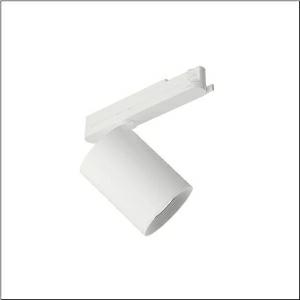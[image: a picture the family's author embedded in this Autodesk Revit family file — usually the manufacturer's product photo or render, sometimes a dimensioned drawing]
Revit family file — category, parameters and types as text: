
# Revit family: spot_21_51se12mba5b
name_source: partatom
category: Lighting Fixtures
units: mm (PartAtom-declared; Revit-internal decimal feet)

## family parameters
Cut with Voids When Loaded = No
Host = Face
Light Source = No
Part Type = Normal
Room Calculation Point = No
Round Connector Dimension = Use Diameter
Shared = No

## types (1)
- --- (1 x LED, 5240 lm, 41.7 W, 2700K)
    Apparent Load = 42 VA
    CIE Flux Codes = 95 98 99 100 100
    Color Rendering = 90
    Color Temperature = 2700K
    Default Elevation = 1800 mm
    Description = Spot 21, directional spotlight, light control with lens, of PMMA, LED rated luminous flux: 5.040lm, light colour: 927, control gear: ECG Multilumen, with 3-phase adapter, mains connection: 220..240V, AC, 50/60Hz, of aluminium, traffic white (RAL 9016), length: 213mm, diameter: 105mm, protection rating (complete): IP20, insulation class (complete): insulation class I (protective earthing), certification: CE, impact resistance: IK02, permissible ambient temperature for indoor applications: -20..+40°C, packaging unit: 1 piece
    Height = 175 mm
    Lamp = 1 x LED
    Lamp Light Flux = 5240 lm
    Lamp Power = 41.7 W
    Lamp count = 1
    Length = 105 mm
    Luminous efficacy = 126 lm/W
    Manufacturer = Siteco
    ModVariant = No
    Model = 51SE12MBA5B
    Mounting Place = Ceiling
    Mounting Type = Pendant
    Number of Poles = 1
    OnlyDefault = Yes
    Power Factor = 1
    Product Name = Spot 21
    Product group = directional spotlight
    ProductGroupID = 905
    Protection Class = Protection class I
    Protection Degree = IP 20
    RLX_Detail_Level = 1
    RLX_Emergency_Light_Flux = 0 lm
    RLX_Emergency_Type = 0
    RLX_Emergency_Type_DB = No
    RlxData = <blob elided: 17641 chars, md5=a18ca57f>
    Socket = socket
    Standby Power = 0 W
    System Light Flux = 5240 lm
    System Power = 42 W
    Type Comments = factory setting: luminous flux: 100 % | (ON | ON | ON | ON) | 1050 mA
    Type Image = l_1003976.jpg
    URL = http://relux.com
    VarID = @adj_165985
    Voltage = 0 V
    Weight = 0.00 kg
    Width = 0 mm  [stored 0 ft]

note: [stored X ft] marks values corroborated as IEEE doubles in the binary element streams (Revit-internal decimal feet)

## geometry (parser evidence)
native form markers: Blend x4, Sweep x9
no freeform markers — native parametric forms only
